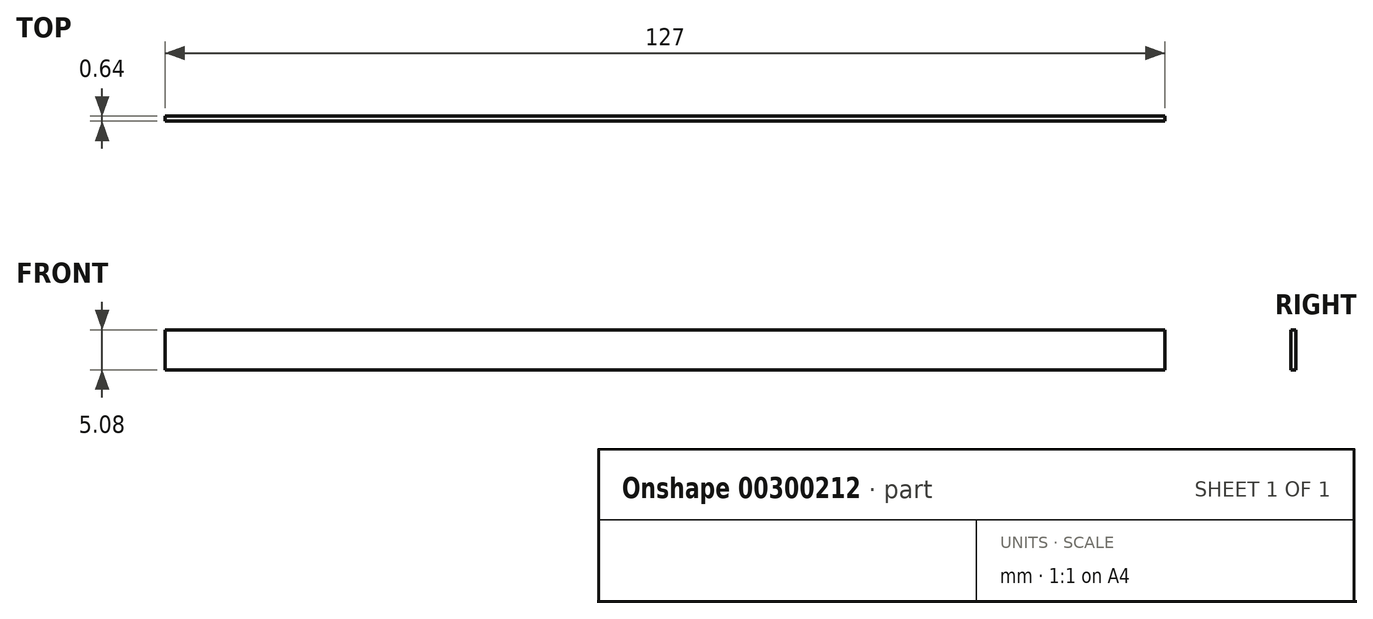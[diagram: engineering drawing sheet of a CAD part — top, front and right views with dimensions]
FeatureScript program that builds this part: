
annotation { "Feature Type Name" : "Feature", "Feature Type Description" : "" }
export const myFeature = defineFeature(function(context is Context, id is Id, definition is map)
    precondition{}
    {
        {
            var Q0;
            Q0=qCreatedBy(makeId("Right.planeOp"),FACE);
            var sketch = newSketch(context, id + "F0", { "sketchPlane" : qUnion([Q0])});
            skLineSegment(sketch, "E0.bottom", {"start": v(-36.15, 36.85) * mm, "end": v(-35.51, 36.85) * mm});
            skLineSegment(sketch, "E0.top", {"start": v(-36.15, 31.77) * mm, "end": v(-35.51, 31.77) * mm});
            skLineSegment(sketch, "E0.left", {"start": v(-36.15, 36.85) * mm, "end": v(-36.15, 31.77) * mm});
            skLineSegment(sketch, "E0.right", {"start": v(-35.51, 36.85) * mm, "end": v(-35.51, 31.77) * mm});
            skSolve(sketch);
        }
        {
            var Q0;
            Q0=makeQuery(id+"F0.imprint","IMPRINT",FACE,{"disambiguationData":[TD([[makeQuery(id+"F0.imprint","IMPRINT",EDGE,{"derivedFrom":sQuery(id+"F0.wireOp",EDGE,"E0.bottom")}),-1.0]])]});
            extrude(context, id + "F1", {"entities" : qUnion([Q0]), "depth" : 127 * mm});
        }
    });
